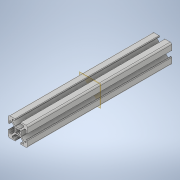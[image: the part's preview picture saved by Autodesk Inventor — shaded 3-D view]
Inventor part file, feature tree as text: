
AUTODESK INVENTOR PART (.ipt)
format: ipt  version: 2022 (Build 260153000, 153)  size: 246,272 bytes
history: native  units: mm
features: extrude x1, sketch x1
ambient origin geometry x8: Origin, YZ Plane, XZ Plane, XY Plane, X Axis, Y Axis, Z Axis, Center Point
bodies: Solid1 (feature_tree)
feature tree (2):
  extrude  "Extrusion1"  Depth=150.0mm
  sketch  "Sketch_1"  dims[d0=150.0mm d1=0.0mm d2=0.5mm d3=0.872665mm d4=0.5mm d5=0.872665mm]
